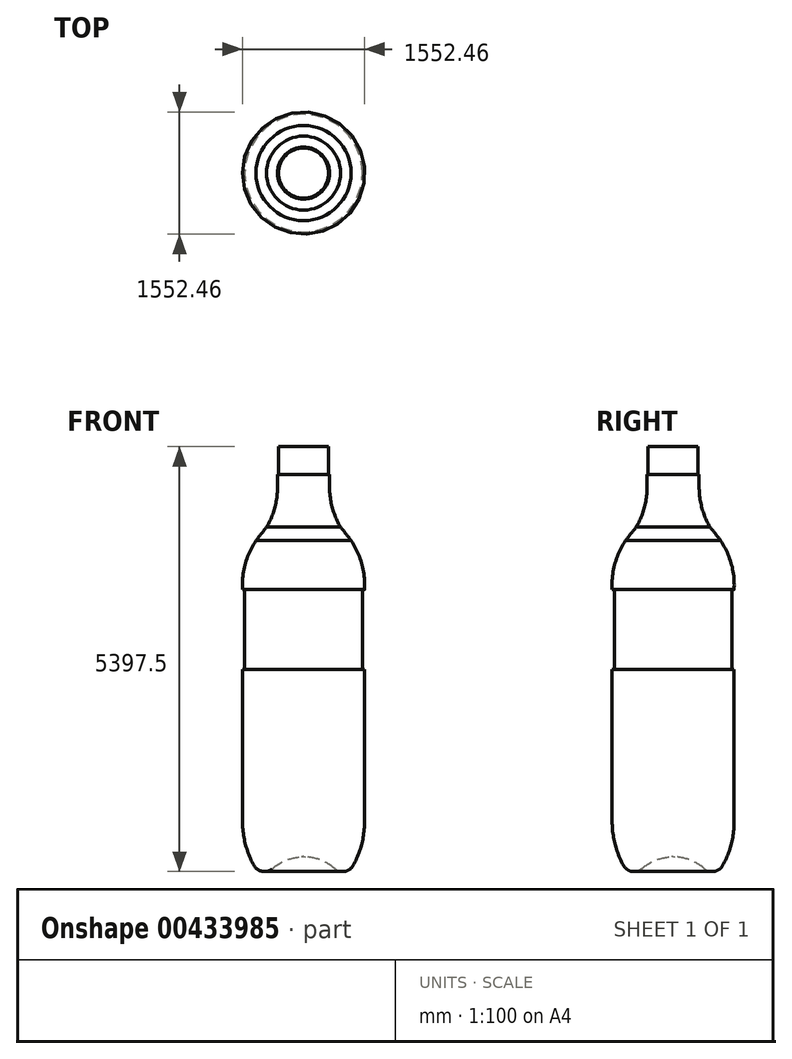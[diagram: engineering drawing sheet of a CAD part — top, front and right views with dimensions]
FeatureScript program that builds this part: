
annotation { "Feature Type Name" : "Feature", "Feature Type Description" : "" }
export const myFeature = defineFeature(function(context is Context, id is Id, definition is map)
    precondition{}
    {
        {
            var Q0;
            Q0=qCreatedBy(makeId("Front.planeOp"),FACE);
            var sketch = newSketch(context, id + "F0", { "sketchPlane" : qUnion([Q0])});
            skLineSegment(sketch, "E0", {"start": v(-182.7, 5282.85) * mm, "end": v(-500.2, 5282.85) * mm});
            skLineSegment(sketch, "E1", {"start": v(-500.2, 5282.85) * mm, "end": v(-500.2, 4927.25) * mm});
            skPoint(sketch, "E2.centerSnap0", {"position": v(-825.03, 287.03) * mm});
            skPoint(sketch, "E3.centerSnap0", {"position": v(-1203.3, 239.55) * mm});
            skArc(sketch, "E4", {"start": v(-957.4, 520.35) * mm, "mid": v(-920.61, 232.67) * mm, "end": v(-812.6, -36.5) * mm});
            skArc(sketch, "E5", {"start": v(-812.6, -36.5) * mm, "mid": v(-706.15, -112.3) * mm, "end": v(-580.1, -77.78) * mm});
            skArc(sketch, "E6", {"start": v(-206.14, 74.58) * mm, "mid": v(-405.56, 28.92) * mm, "end": v(-580.1, -77.78) * mm});
            skLineSegment(sketch, "E7", {"start": v(-957.4, 520.35) * mm, "end": v(-957.4, 2452.78) * mm});
            skLineSegment(sketch, "E8", {"start": v(-957.4, 2452.78) * mm, "end": v(-929.47, 2452.78) * mm});
            skLineSegment(sketch, "E9", {"start": v(-929.47, 2452.78) * mm, "end": v(-929.47, 3468.78) * mm});
            skLineSegment(sketch, "E10", {"start": v(-929.47, 3468.78) * mm, "end": v(-957.4, 3468.78) * mm});
            skLineSegment(sketch, "E11", {"start": v(-182.7, 75.85) * mm, "end": v(-182.7, 5282.85) * mm});
            skLineSegment(sketch, "E12", {"start": v(-500.2, 4927.25) * mm, "end": v(-512.9, 4927.25) * mm});
            skLineSegment(sketch, "E13", {"start": v(-512.9, 4927.25) * mm, "end": v(-512.9, 4774.85) * mm});
            skArc(sketch, "E14", {"start": v(-652.23, 4261.35) * mm, "mid": v(-548.36, 4508.82) * mm, "end": v(-512.9, 4774.85) * mm});
            skArc(sketch, "E15", {"start": v(-652.23, 4261.35) * mm, "mid": v(-720.36, 4176.69) * mm, "end": v(-786.66, 4090.6) * mm});
            skArc(sketch, "E16", {"start": v(-786.66, 4090.6) * mm, "mid": v(-922.67, 3793.6) * mm, "end": v(-957.4, 3468.78) * mm});
            skLineSegment(sketch, "E17", {"start": v(-206.14, 74.58) * mm, "end": v(-182.7, 75.85) * mm});
            skSolve(sketch);
        }
        {
            var Q0;
            Q0=makeQuery(id+"F0.imprint","IMPRINT",FACE,{"disambiguationData":[TD([[makeQuery(id+"F0.imprint","IMPRINT",EDGE,{"derivedFrom":sQuery(id+"F0.wireOp",EDGE,"E0")}),1.0]])]});
            var Q1;
            Q1=sQuery(id+"F0.wireOp",EDGE,"E11");
            revolve(context, id + "F1", {"entities" : qUnion([Q0]), "axis" : qUnion([Q1]), "revolveType" : RevolveType.FULL});
        }
    });
